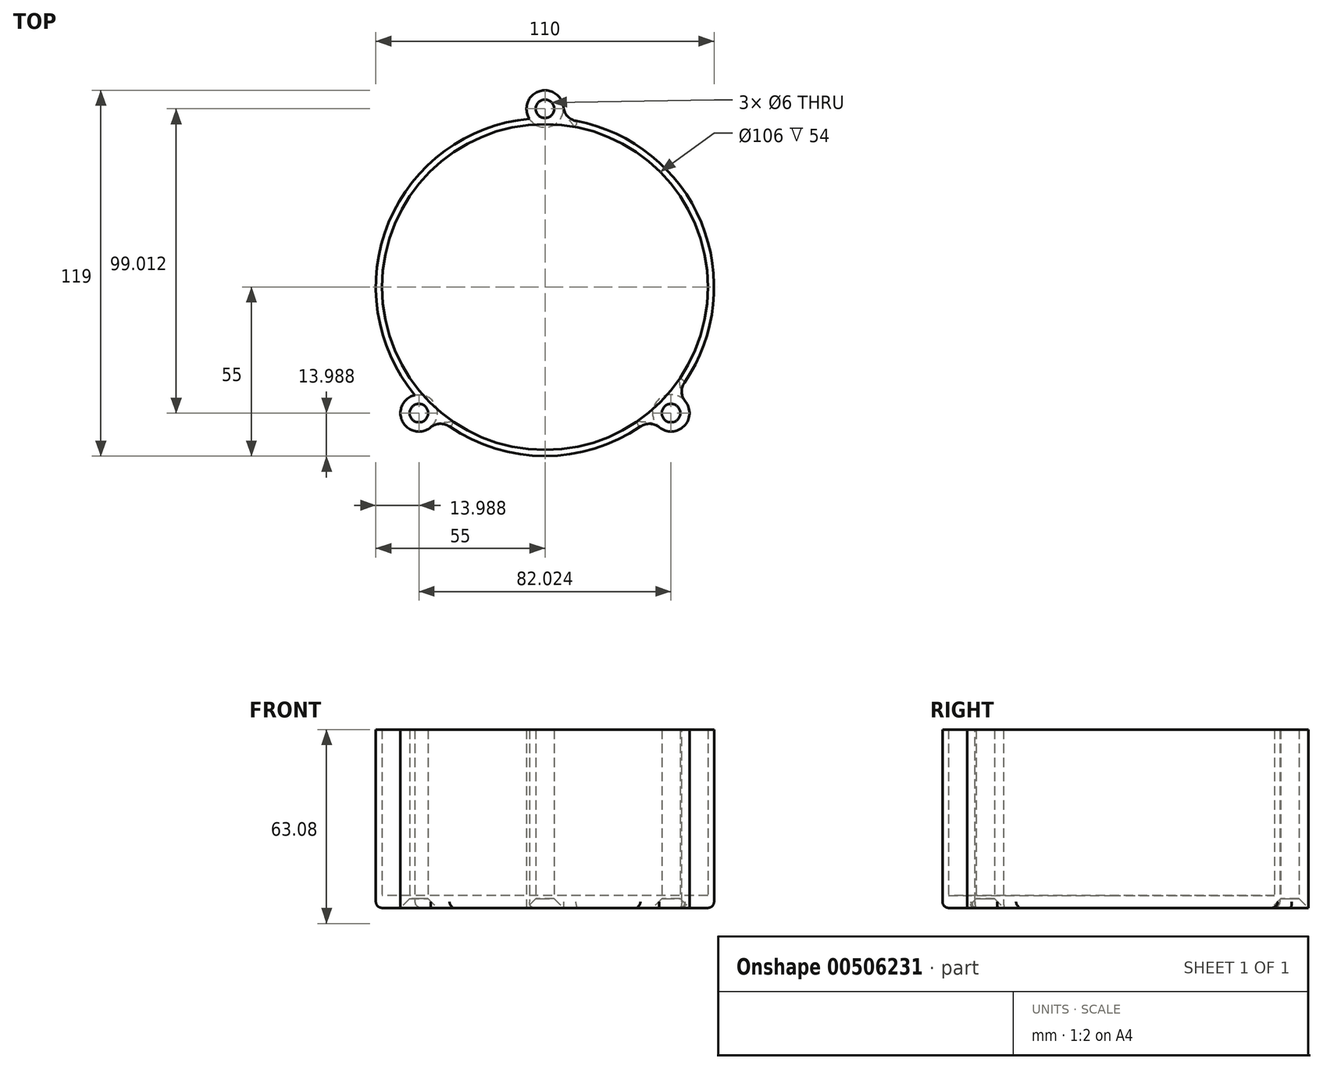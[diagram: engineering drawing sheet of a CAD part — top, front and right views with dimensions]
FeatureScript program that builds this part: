
annotation { "Feature Type Name" : "Feature", "Feature Type Description" : "" }
export const myFeature = defineFeature(function(context is Context, id is Id, definition is map)
    precondition{}
    {
        {
            var Q0;
            Q0=qCreatedBy(makeId("Top.planeOp"),FACE);
            var sketch = newSketch(context, id + "F0", { "sketchPlane" : qUnion([Q0])});
            skCircle(sketch, "E0", {"center": v(0, 58) * mm, "radius": 3 * mm});
            skArc(sketch, "E1", {"start": v(5.05, 54.77) * mm, "mid": v(0, 64) * mm, "end": v(-5.05, 54.77) * mm});
            skCircle(sketch, "E2", {"center": v(-41.01, -41.01) * mm, "radius": 3 * mm});
            skArc(sketch, "E3", {"start": v(-42.3, -35.15) * mm, "mid": v(-45.25, -45.25) * mm, "end": v(-35.15, -42.3) * mm});
            skCircle(sketch, "E4", {"center": v(41.01, -41.01) * mm, "radius": 3 * mm});
            skArc(sketch, "E5", {"start": v(35.15, -42.3) * mm, "mid": v(45.25, -45.25) * mm, "end": v(42.3, -35.15) * mm});
            skLineSegment(sketch, "E6", {"start": v(5.05, 54.77) * mm, "end": v(-5.05, 54.77) * mm});
            skLineSegment(sketch, "E7", {"start": v(-42.3, -35.15) * mm, "end": v(-35.15, -42.3) * mm});
            skLineSegment(sketch, "E8", {"start": v(42.3, -35.15) * mm, "end": v(35.15, -42.3) * mm});
            skSolve(sketch);
        }
        {
            var Q0;
            Q0=qCreatedBy(makeId("Top.planeOp"),FACE);
            var sketch = newSketch(context, id + "F1", { "sketchPlane" : qUnion([Q0])});
            skCircle(sketch, "E9", {"center": v(0, 0) * mm, "radius": 53 * mm});
            skCircle(sketch, "E10", {"center": v(0, 0) * mm, "radius": 55 * mm});
            skSolve(sketch);
        }
        {
            var Q0;
            Q0 = qSketchRegion(id + "F1", true);
            extrude(context, id + "F2", {"entities" : qUnion([Q0]), "depth" : 54 * mm});
        }
        {
            var Q0;
            Q0=qCreatedBy(makeId("Top.planeOp"),FACE);
            var sketch = newSketch(context, id + "F3", { "sketchPlane" : qUnion([Q0])});
            skCircle(sketch, "E11", {"center": v(0, 0) * mm, "radius": 55 * mm});
            skSolve(sketch);
        }
        {
            var Q0;
            Q0=makeQuery(id+"F3.imprint","IMPRINT",FACE,{"disambiguationData":[TD([[makeQuery(id+"F3.imprint","IMPRINT",EDGE,{"derivedFrom":sQuery(id+"F3.wireOp",EDGE,"E11")}),1.0]])]});
            extrude(context, id + "F4", {"entities" : qUnion([Q0]), "operationType" : NewBodyOperationType.ADD, "oppositeDirection" : true, "depth" : 4 * mm});
        }
        {
            var Q0;
            Q0=makeQuery(id+"F0.imprint","IMPRINT",FACE,{"disambiguationData":[TD([[makeQuery(id+"F0.imprint","IMPRINT",EDGE,{"derivedFrom":sQuery(id+"F0.wireOp",EDGE,"E0")}),-1.0]])]});
            var Q1;
            Q1=makeQuery(id+"F0.imprint","IMPRINT",FACE,{"disambiguationData":[TD([[makeQuery(id+"F0.imprint","IMPRINT",EDGE,{"derivedFrom":sQuery(id+"F0.wireOp",EDGE,"E2")}),-1.0]])]});
            var Q2;
            Q2=makeQuery(id+"F0.imprint","IMPRINT",FACE,{"disambiguationData":[TD([[makeQuery(id+"F0.imprint","IMPRINT",EDGE,{"derivedFrom":sQuery(id+"F0.wireOp",EDGE,"E4")}),-1.0]])]});
            var Q3;
            Q3=sQuery(id+"F0.wireOp",EDGE,"E1");
            extrude(context, id + "F5", {"entities" : qUnion([Q0, Q1, Q2]), "operationType" : NewBodyOperationType.ADD, "surfaceEntities" : qUnion([Q3]), "depth" : 54 * mm, "hasSecondDirection" : true, "secondDirectionOppositeDirection" : true, "secondDirectionDepth" : 4 * mm});
        }
        {
            var Q0;
            Q0=makeQuery(id+"F5.opExtrude","CAP_EDGE",EDGE,{"disambiguationData":[OSD([sQuery(id+"F0.wireOp",EDGE,"E4")])],"isStart":true});
            var Q1;
            Q1=makeQuery(id+"F5.opExtrude","CAP_EDGE",EDGE,{"disambiguationData":[OSD([sQuery(id+"F0.wireOp",EDGE,"E2")])],"isStart":true});
            var Q2;
            Q2=makeQuery(id+"F5.opExtrude","CAP_EDGE",EDGE,{"disambiguationData":[OSD([sQuery(id+"F0.wireOp",EDGE,"E0")])],"isStart":true});
            chamfer(context, id + "F6", {"entities" : qUnion([Q0, Q1, Q2]), "width" : 3 * mm, "tangentPropagation" : true});
        }
        {
            var Q0;
            {var subQ0=sQuery(id+"F0.wireOp",EDGE,"E1");var subQ1=sQuery(id+"F3.wireOp",EDGE,"E11");var subQ2=sQuery(id+"F0.wireOp",EDGE,"E3");Q0=makeQuery(id+"F5.boolean.opBoolean","SPLIT",EDGE,{"disambiguationData":[TD([makeQuery(id+"F2.opExtrude","SWEPT_FACE",FACE,{"disambiguationData":[OSD([sQuery(id+"F1.wireOp",EDGE,"E10")])]}),makeQuery(id+"F4.opExtrude","SWEPT_FACE",FACE,{"disambiguationData":[OSD([subQ1])]}),makeQuery(id+"F4.opExtrude","CAP_FACE",FACE,{"disambiguationData":[OSD([subQ1])],"isStart":false}),makeQuery(id+"F5.opExtrude","CAP_FACE",FACE,{"disambiguationData":[OSD([sQuery(id+"F0.wireOp",EDGE,"E0"),subQ0,sQuery(id+"F0.wireOp",EDGE,"E6")])],"isStart":true}),makeQuery(id+"F5.opExtrude","SWEPT_FACE",FACE,{"disambiguationData":[OSD([subQ0])]}),makeQuery(id+"F5.opExtrude","CAP_FACE",FACE,{"disambiguationData":[OSD([sQuery(id+"F0.wireOp",EDGE,"E2"),subQ2,sQuery(id+"F0.wireOp",EDGE,"E7")])],"isStart":true}),makeQuery(id+"F5.opExtrude","SWEPT_FACE",FACE,{"disambiguationData":[OSD([subQ2])]}),makeQuery(id+"F5.opExtrude","CAP_FACE",FACE,{"disambiguationData":[OSD([sQuery(id+"F0.wireOp",EDGE,"E4"),sQuery(id+"F0.wireOp",EDGE,"E5"),sQuery(id+"F0.wireOp",EDGE,"E8")])],"isStart":true})])],"derivedFrom":makeQuery(id+"F4.opExtrude","CAP_EDGE",EDGE,{"disambiguationData":[OSD([subQ1])],"isStart":false})});}
            var Q1;
            {var subQ0=sQuery(id+"F3.wireOp",EDGE,"E11");var subQ1=sQuery(id+"F0.wireOp",EDGE,"E3");var subQ2=sQuery(id+"F0.wireOp",EDGE,"E5");Q1=makeQuery(id+"F5.boolean.opBoolean","SPLIT",EDGE,{"disambiguationData":[TD([makeQuery(id+"F2.opExtrude","SWEPT_FACE",FACE,{"disambiguationData":[OSD([sQuery(id+"F1.wireOp",EDGE,"E10")])]}),makeQuery(id+"F4.opExtrude","SWEPT_FACE",FACE,{"disambiguationData":[OSD([subQ0])]}),makeQuery(id+"F4.opExtrude","CAP_FACE",FACE,{"disambiguationData":[OSD([subQ0])],"isStart":false}),makeQuery(id+"F5.opExtrude","CAP_FACE",FACE,{"disambiguationData":[OSD([sQuery(id+"F0.wireOp",EDGE,"E0"),sQuery(id+"F0.wireOp",EDGE,"E1"),sQuery(id+"F0.wireOp",EDGE,"E6")])],"isStart":true}),makeQuery(id+"F5.opExtrude","CAP_FACE",FACE,{"disambiguationData":[OSD([sQuery(id+"F0.wireOp",EDGE,"E2"),subQ1,sQuery(id+"F0.wireOp",EDGE,"E7")])],"isStart":true}),makeQuery(id+"F5.opExtrude","SWEPT_FACE",FACE,{"disambiguationData":[OSD([subQ1])]}),makeQuery(id+"F5.opExtrude","CAP_FACE",FACE,{"disambiguationData":[OSD([sQuery(id+"F0.wireOp",EDGE,"E4"),subQ2,sQuery(id+"F0.wireOp",EDGE,"E8")])],"isStart":true}),makeQuery(id+"F5.opExtrude","SWEPT_FACE",FACE,{"disambiguationData":[OSD([subQ2])]})])],"derivedFrom":makeQuery(id+"F4.opExtrude","CAP_EDGE",EDGE,{"disambiguationData":[OSD([subQ0])],"isStart":false})});}
            var Q2;
            {var subQ0=sQuery(id+"F0.wireOp",EDGE,"E1");var subQ1=sQuery(id+"F3.wireOp",EDGE,"E11");var subQ2=sQuery(id+"F0.wireOp",EDGE,"E5");Q2=makeQuery(id+"F5.boolean.opBoolean","SPLIT",EDGE,{"disambiguationData":[TD([makeQuery(id+"F2.opExtrude","SWEPT_FACE",FACE,{"disambiguationData":[OSD([sQuery(id+"F1.wireOp",EDGE,"E10")])]}),makeQuery(id+"F4.opExtrude","SWEPT_FACE",FACE,{"disambiguationData":[OSD([subQ1])]}),makeQuery(id+"F4.opExtrude","CAP_FACE",FACE,{"disambiguationData":[OSD([subQ1])],"isStart":false}),makeQuery(id+"F5.opExtrude","CAP_FACE",FACE,{"disambiguationData":[OSD([sQuery(id+"F0.wireOp",EDGE,"E0"),subQ0,sQuery(id+"F0.wireOp",EDGE,"E6")])],"isStart":true}),makeQuery(id+"F5.opExtrude","SWEPT_FACE",FACE,{"disambiguationData":[OSD([subQ0])]}),makeQuery(id+"F5.opExtrude","CAP_FACE",FACE,{"disambiguationData":[OSD([sQuery(id+"F0.wireOp",EDGE,"E2"),sQuery(id+"F0.wireOp",EDGE,"E3"),sQuery(id+"F0.wireOp",EDGE,"E7")])],"isStart":true}),makeQuery(id+"F5.opExtrude","CAP_FACE",FACE,{"disambiguationData":[OSD([sQuery(id+"F0.wireOp",EDGE,"E4"),subQ2,sQuery(id+"F0.wireOp",EDGE,"E8")])],"isStart":true}),makeQuery(id+"F5.opExtrude","SWEPT_FACE",FACE,{"disambiguationData":[OSD([subQ2])]})])],"derivedFrom":makeQuery(id+"F4.opExtrude","CAP_EDGE",EDGE,{"disambiguationData":[OSD([subQ1])],"isStart":false})});}
            fillet(context, id + "F7", {"entities" : qUnion([Q0, Q1, Q2]), "radius" : 2 * mm, "tangentPropagation" : true, "allowEdgeOverflow" : false});
        }
        {
            var Q0;
            {var subQ0=sQuery(id+"F0.wireOp",EDGE,"E6");var subQ1=sQuery(id+"F0.wireOp",EDGE,"E1");Q0=makeQuery(id+"F5.opExtrude","SWEPT_EDGE",EDGE,{"disambiguationData":[OSD([subQ1,subQ0]),TDD([makeQuery(id+"F0.imprint","INTERSECT",VERTEX,{"disambiguationData":[OD(1.0)],"derivedFrom":[subQ1,subQ0]})])]});}
            var Q1;
            {var subQ0=sQuery(id+"F0.wireOp",EDGE,"E6");var subQ1=sQuery(id+"F0.wireOp",EDGE,"E1");Q1=makeQuery(id+"F5.opExtrude","SWEPT_EDGE",EDGE,{"disambiguationData":[OSD([subQ1,subQ0]),TDD([makeQuery(id+"F0.imprint","INTERSECT",VERTEX,{"disambiguationData":[OD(0.0)],"derivedFrom":[subQ1,subQ0]})])]});}
            var Q2;
            {var subQ0=sQuery(id+"F0.wireOp",EDGE,"E8");var subQ1=sQuery(id+"F0.wireOp",EDGE,"E5");Q2=makeQuery(id+"F5.opExtrude","SWEPT_EDGE",EDGE,{"disambiguationData":[OSD([subQ1,subQ0]),TDD([makeQuery(id+"F0.imprint","INTERSECT",VERTEX,{"disambiguationData":[OD(1.0)],"derivedFrom":[subQ1,subQ0]})])]});}
            var Q3;
            {var subQ0=sQuery(id+"F0.wireOp",EDGE,"E8");var subQ1=sQuery(id+"F0.wireOp",EDGE,"E5");Q3=makeQuery(id+"F5.opExtrude","SWEPT_EDGE",EDGE,{"disambiguationData":[OSD([subQ1,subQ0]),TDD([makeQuery(id+"F0.imprint","INTERSECT",VERTEX,{"disambiguationData":[OD(0.0)],"derivedFrom":[subQ1,subQ0]})])]});}
            var Q4;
            {var subQ0=sQuery(id+"F0.wireOp",EDGE,"E7");var subQ1=sQuery(id+"F0.wireOp",EDGE,"E3");Q4=makeQuery(id+"F5.opExtrude","SWEPT_EDGE",EDGE,{"disambiguationData":[OSD([subQ1,subQ0]),TDD([makeQuery(id+"F0.imprint","INTERSECT",VERTEX,{"disambiguationData":[OD(1.0)],"derivedFrom":[subQ1,subQ0]})])]});}
            var Q5;
            {var subQ0=sQuery(id+"F0.wireOp",EDGE,"E7");var subQ1=sQuery(id+"F0.wireOp",EDGE,"E3");Q5=makeQuery(id+"F5.opExtrude","SWEPT_EDGE",EDGE,{"disambiguationData":[OSD([subQ1,subQ0]),TDD([makeQuery(id+"F0.imprint","INTERSECT",VERTEX,{"disambiguationData":[OD(0.0)],"derivedFrom":[subQ1,subQ0]})])]});}
            fillet(context, id + "F8", {"entities" : qUnion([Q0, Q1, Q2, Q3, Q4, Q5]), "radius" : 5.08 * mm, "tangentPropagation" : true, "allowEdgeOverflow" : false});
        }
    });
